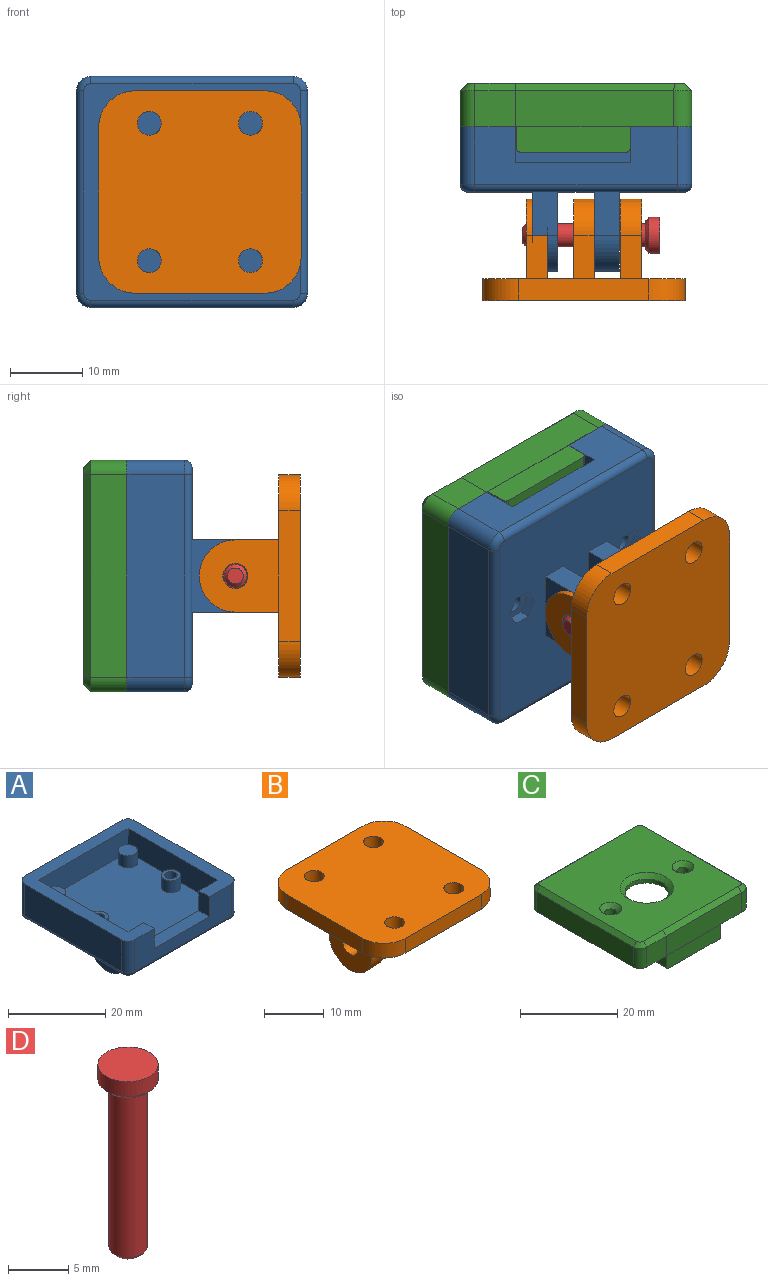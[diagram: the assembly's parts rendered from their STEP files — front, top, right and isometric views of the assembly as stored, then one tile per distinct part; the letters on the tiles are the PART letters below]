
ASSEMBLY  parts=4 mates=3
PART A: 62 faces, bbox 32.3x32.3x20 mm
  f0: plane 30x30mm, normal (0,0,-1), area 798.6mm2, adj f28,f29,f30,f31,f32,f33,f34,f35
  f1: cylinder r=1.25mm len=4.5mm, axis (0,0,-1), area 35.3mm2, adj f14,f61
  f2: cylinder r=1.25mm len=4.5mm, axis (0,0,-1), area 35.3mm2, adj f16,f54
  f3: plane 32x32mm, normal (0,0,1), area 296.6mm2, adj f4,f6,f7,f8,f9,f10,f11,f12
  f4: plane 28x8mm, normal (0,-1,0), area 144mm2, adj f3,f21,f22,f23,f26,f27,f44
  f5: plane 26x26mm, normal (0,0,1), area 625.7mm2, adj f6,f7,f8,f9,f13,f15,f17,f19
  f6: plane 26x6mm, normal (0,-1,0), area 156mm2, adj f3,f5,f7,f9
  f7: plane 26x6mm, normal (1,0,0), area 156mm2, adj f3,f5,f6,f8
  f8: plane 26x6mm, normal (0,1,0), area 76mm2, adj f3,f5,f7,f9,f21,f22,f23
  f9: plane 26x6mm, normal (-1,0,0), area 156mm2, adj f3,f5,f6,f8
  f10: plane 28x8mm, normal (1,0,0), area 224mm2, adj f3,f24,f27,f40
  f11: plane 28x8mm, normal (0,1,0), area 224mm2, adj f3,f24,f25,f43
  f12: plane 28x8mm, normal (-1,0,0), area 224mm2, adj f3,f25,f26,f47
  f13: cylinder r=2mm len=4mm, axis (0,0,-1), area 37.7mm2, adj f5,f14
  f14: plane 4x4mm, normal (0,0,1), area 7.7mm2, adj f1,f13
  f15: cylinder r=2mm len=4mm, axis (0,0,-1), area 37.7mm2, adj f5,f16
  f16: plane 4x4mm, normal (0,0,1), area 7.7mm2, adj f2,f15
  f17: cylinder r=2mm len=4mm, axis (0,0,-1), area 37.7mm2, adj f5,f18
  f18: plane 4x4mm, normal (0,0,1), area 12.6mm2, adj f17
  f19: cylinder r=2mm len=4mm, axis (0,0,-1), area 37.7mm2, adj f5,f20
  f20: plane 4x4mm, normal (0,0,1), area 12.6mm2, adj f19
  f21: plane 5x3mm, normal (1,0,0), area 15mm2, adj f3,f4,f8,f22
  f22: plane 16x3mm, normal (0,0,1), area 48mm2, adj f4,f8,f21,f23
  f23: plane 5x3mm, normal (-1,0,0), area 15mm2, adj f3,f4,f8,f22
  f24: cylinder r=2mm len=8mm, axis (0,0,-1), area 25.1mm2, adj f3,f10,f11,f41
  f25: cylinder r=2mm len=8mm, axis (0,0,1), area 25.1mm2, adj f3,f11,f12,f45
  f26: cylinder r=2mm len=8mm, axis (0,0,-1), area 25.1mm2, adj f3,f4,f12,f46
  f27: cylinder r=2mm len=8mm, axis (0,0,1), area 25.1mm2, adj f3,f4,f10,f42
  f28: plane 11x10mm, normal (1,0,0), area 89.6mm2, adj f0,f29,f31,f36,f39
  f29: plane 6x3.5mm, normal (0,1,0), area 21mm2, adj f0,f28,f30,f36
  f30: plane 11x10mm, normal (-1,0,0), area 89.6mm2, adj f0,f29,f31,f36,f39
  f31: plane 6x3.5mm, normal (0,-1,0), area 21mm2, adj f0,f28,f30,f36
  f32: plane 11x10mm, normal (1,0,0), area 89.6mm2, adj f0,f33,f35,f37,f38
  f33: plane 6x3.5mm, normal (0,1,0), area 21mm2, adj f0,f32,f34,f37
  f34: plane 11x10mm, normal (-1,0,0), area 89.6mm2, adj f0,f33,f35,f37,f38
  f35: plane 6x3.5mm, normal (0,-1,0), area 21mm2, adj f0,f32,f34,f37
  f36: cylinder r=5mm len=10mm, axis (-1,0,0), area 55mm2, adj f28,f29,f30,f31
  f37: cylinder r=5mm len=10mm, axis (-1,0,0), area 55mm2, adj f32,f33,f34,f35
  f38: cylinder r=1.75mm len=3.5mm, axis (1,0,0), area 38.5mm2, adj f32,f34
  f39: cylinder r=1.75mm len=3.5mm, axis (1,0,0), area 38.5mm2, adj f28,f30
  f40: cylinder r=1mm len=28mm, axis (0,1,0), area 44mm2, adj f0,f10,f41,f42
  f41: torus R=1mm, axis (0,0,1), area 4mm2, adj f0,f24,f40,f43
  f42: torus R=1mm, axis (0,0,1), area 4mm2, adj f0,f27,f40,f44
  f43: cylinder r=1mm len=28mm, axis (-1,0,0), area 44mm2, adj f0,f11,f41,f45
  f44: cylinder r=1mm len=28mm, axis (1,0,0), area 44mm2, adj f0,f4,f42,f46
  f45: torus R=1mm, axis (0,0,1), area 4mm2, adj f0,f25,f43,f47
  f46: torus R=1mm, axis (0,0,1), area 4mm2, adj f0,f26,f44,f47
  f47: cylinder r=1mm len=28mm, axis (0,-1,0), area 44mm2, adj f0,f12,f45,f46
  f48: plane 2.43x1.5mm, normal (0,1,0), area 3.6mm2, adj f0,f49,f53,f54
  f49: plane 2.1x1.5mm, normal (0.87,0.5,0), area 3.6mm2, adj f0,f48,f50,f54
  f50: plane 2.1x1.5mm, normal (0.87,-0.5,0), area 3.6mm2, adj f0,f49,f51,f54
  f51: plane 2.43x1.5mm, normal (0,-1,0), area 3.6mm2, adj f0,f50,f52,f54
  f52: plane 2.1x1.5mm, normal (-0.87,-0.5,0), area 3.6mm2, adj f0,f51,f53,f54
  f53: plane 2.1x1.5mm, normal (-0.87,0.5,0), area 3.6mm2, adj f0,f48,f52,f54
  f54: plane 4.85x4.2mm, normal (0,0,-1), area 10.4mm2, adj f2,f48,f49,f50,f51,f52,f53
  f55: plane 2.43x1.5mm, normal (0,1,0), area 3.6mm2, adj f0,f56,f60,f61
  f56: plane 2.1x1.5mm, normal (0.87,0.5,0), area 3.6mm2, adj f0,f55,f57,f61
  f57: plane 2.1x1.5mm, normal (0.87,-0.5,0), area 3.6mm2, adj f0,f56,f58,f61
  f58: plane 2.43x1.5mm, normal (0,-1,0), area 3.6mm2, adj f0,f57,f59,f61
  f59: plane 2.1x1.5mm, normal (-0.87,-0.5,0), area 3.6mm2, adj f0,f58,f60,f61
  f60: plane 2.1x1.5mm, normal (-0.87,0.5,0), area 3.6mm2, adj f0,f55,f59,f61
  f61: plane 4.85x4.2mm, normal (0,0,-1), area 10.4mm2, adj f1,f55,f56,f57,f58,f59,f60
PART B: 32 faces, bbox 28x28x14 mm
  f0: plane 18x3mm, normal (0,-1,0), area 54mm2, adj f4,f5,f28,f31
  f1: plane 18x3mm, normal (1,0,0), area 54mm2, adj f4,f5,f28,f29
  f2: plane 18x3mm, normal (0,1,0), area 54mm2, adj f4,f5,f29,f30
  f3: plane 18x3mm, normal (-1,0,0), area 54mm2, adj f4,f5,f30,f31
  f4: plane 28x28mm, normal (0,0,-1), area 640.3mm2, adj f0,f1,f2,f3,f6,f7,f8,f9
  f5: plane 28x28mm, normal (0,0,1), area 728.3mm2, adj f0,f1,f2,f3,f24,f25,f26,f27
  f6: plane 6x2.8mm, normal (0,-1,0), area 16.8mm2, adj f4,f7,f9,f19
  f7: plane 11x10mm, normal (-1,0,0), area 89.6mm2, adj f4,f6,f8,f19,f23
  f8: plane 6x2.8mm, normal (0,1,0), area 16.8mm2, adj f4,f7,f9,f19
  f9: plane 11x10mm, normal (1,0,0), area 89.6mm2, adj f4,f6,f8,f19,f23
  f10: plane 11x10mm, normal (1,0,0), area 89.6mm2, adj f4,f11,f13,f20,f22
  f11: plane 6x3mm, normal (0,-1,0), area 18mm2, adj f4,f10,f12,f20
  f12: plane 11x10mm, normal (-1,0,0), area 89.6mm2, adj f4,f11,f13,f20,f22
  f13: plane 6x3mm, normal (0,1,0), area 18mm2, adj f4,f10,f12,f20
  f14: plane 6x3mm, normal (0,-1,0), area 18mm2, adj f4,f15,f17,f18
  f15: plane 11x10mm, normal (-1,0,0), area 89.6mm2, adj f4,f14,f16,f18,f21
  f16: plane 6x3mm, normal (0,1,0), area 18mm2, adj f4,f15,f17,f18
  f17: plane 11x10mm, normal (1,0,0), area 89.6mm2, adj f4,f14,f16,f18,f21
  f18: cylinder r=5mm len=10mm, axis (1,0,0), area 47.1mm2, adj f14,f15,f16,f17
  f19: cylinder r=5mm len=10mm, axis (1,0,0), area 44mm2, adj f6,f7,f8,f9
  f20: cylinder r=5mm len=10mm, axis (-1,0,0), area 47.1mm2, adj f10,f11,f12,f13
  f21: cylinder r=1.75mm len=3.5mm, axis (1,0,0), area 33mm2, adj f15,f17
  f22: cylinder r=1.75mm len=3.5mm, axis (1,0,0), area 33mm2, adj f10,f12
  f23: cylinder r=1.75mm len=3.5mm, axis (1,0,0), area 30.8mm2, adj f7,f9
  f24: cylinder r=1.65mm len=3.3mm, axis (0,0,-1), area 31.1mm2, adj f4,f5
  f25: cylinder r=1.65mm len=3.3mm, axis (0,0,-1), area 31.1mm2, adj f4,f5
  f26: cylinder r=1.65mm len=3.3mm, axis (0,0,-1), area 31.1mm2, adj f4,f5
  f27: cylinder r=1.65mm len=3.3mm, axis (0,0,-1), area 31.1mm2, adj f4,f5
  f28: cylinder r=5mm len=5mm, axis (0,0,-1), area 23.6mm2, adj f0,f1,f4,f5
  f29: cylinder r=5mm len=5mm, axis (0,0,1), area 23.6mm2, adj f1,f2,f4,f5
  f30: cylinder r=5mm len=5mm, axis (0,0,-1), area 23.6mm2, adj f2,f3,f4,f5
  f31: cylinder r=5mm len=5mm, axis (0,0,1), area 23.6mm2, adj f0,f3,f4,f5
PART C: 48 faces, bbox 32x32x9.5 mm
  f0: cylinder r=4.5mm len=9mm, axis (0,0,1), area 28.3mm2, adj f28,f40
  f1: plane 26x26mm, normal (0,0,-1), area 398.8mm2, adj f3,f4,f5,f14,f17,f20,f23,f25
  f2: plane 30x30mm, normal (0,0,1), area 771.6mm2, adj f29,f30,f31,f32,f33,f34,f35,f36
  f3: plane 26x3mm, normal (0,-1,0), area 78mm2, adj f1,f4,f5,f16
  f4: plane 26x3mm, normal (1,0,0), area 78mm2, adj f1,f3,f14,f16
  f5: plane 26x3mm, normal (-1,0,0), area 78mm2, adj f1,f3,f14,f16
  f6: plane 28x5mm, normal (1,0,0), area 140mm2, adj f7,f15,f16,f35
  f7: cylinder r=2mm len=5mm, axis (0,0,1), area 15.7mm2, adj f6,f8,f16,f33
  f8: plane 28x5mm, normal (0,1,0), area 140mm2, adj f7,f9,f16,f31
  f9: cylinder r=2mm len=5mm, axis (0,0,1), area 15.7mm2, adj f8,f10,f16,f32
  f10: plane 28x5mm, normal (-1,0,0), area 140mm2, adj f9,f11,f16,f34
  f11: cylinder r=2mm len=5mm, axis (0,0,1), area 15.7mm2, adj f10,f12,f16,f36
  f12: plane 5.6x5mm, normal (0,-1,0), area 28mm2, adj f11,f13,f16,f38
  f13: plane 21.92x5mm, normal (0,-1,0), area 109.6mm2, adj f12,f15,f16,f39,f41
  f14: plane 26x6.5mm, normal (0,1,0), area 132.8mm2, adj f1,f4,f5,f16,f43,f44,f45,f46
  f15: cylinder r=2mm len=5mm, axis (0,0,1), area 18.2mm2, adj f6,f13,f16,f37
  f16: plane 32x32mm, normal (0,0,-1), area 297.1mm2, adj f3,f4,f5,f6,f7,f8,f9,f10
  f17: cylinder r=2mm len=5mm, axis (0,0,1), area 62.8mm2, adj f1,f19
  f18: cylinder r=1.25mm len=7mm, axis (0,0,1), area 55mm2, adj f19,f30
  f19: plane 4x4mm, normal (0,0,-1), area 7.7mm2, adj f17,f18
  f20: cylinder r=2mm len=5mm, axis (0,0,1), area 62.8mm2, adj f1,f22
  f21: cylinder r=1.25mm len=7mm, axis (0,0,1), area 55mm2, adj f22,f29
  f22: plane 4x4mm, normal (0,0,-1), area 7.7mm2, adj f20,f21
  f23: cylinder r=2mm len=5mm, axis (0,0,1), area 62.8mm2, adj f1,f24
  f24: plane 4x4mm, normal (0,0,-1), area 12.6mm2, adj f23
  f25: cylinder r=2mm len=5mm, axis (0,0,1), area 62.8mm2, adj f1,f26
  f26: plane 4x4mm, normal (0,0,-1), area 12.6mm2, adj f25
  f27: cylinder r=8.5mm len=17mm, axis (0,0,-1), area 53.4mm2, adj f1,f28
  f28: plane 17x17mm, normal (0,0,-1), area 163.4mm2, adj f0,f27
  f29: cone r=1.25mm half-angle=45deg, axis (0,0,1), area 15.6mm2, adj f2,f21
  f30: cone r=1.25mm half-angle=45deg, axis (0,0,1), area 15.6mm2, adj f2,f18
  f31: plane 28x1mm, normal (0,0.71,0.71), area 39.6mm2, adj f2,f8,f32,f33
  f32: cone r=1mm half-angle=45deg, axis (0,0,-1), area 3.3mm2, adj f2,f9,f31,f34
  f33: cone r=1mm half-angle=45deg, axis (0,0,-1), area 3.3mm2, adj f2,f7,f31,f35
  f34: plane 28x1mm, normal (-0.71,0,0.71), area 39.6mm2, adj f2,f10,f32,f36
  f35: plane 28x1mm, normal (0.71,0,0.71), area 39.6mm2, adj f2,f6,f33,f37
  f36: cone r=1mm half-angle=45deg, axis (0,0,-1), area 3.3mm2, adj f2,f11,f34,f38
  f37: cone r=1mm half-angle=45deg, axis (0,0,-1), area 3.9mm2, adj f2,f15,f35,f39
  f38: plane 5.6x1mm, normal (0,-0.71,0.71), area 7.9mm2, adj f2,f12,f36,f39
  f39: plane 22.1x1.1mm, normal (0,-0.71,0.71), area 31.1mm2, adj f2,f13,f37,f38
  f40: cone r=4.5mm half-angle=45deg, axis (0,0,1), area 44.4mm2, adj f0,f2
  f41: plane 15.7x0.04mm, normal (0,0,1), area 0.3mm2, adj f13,f42,f44
  f42: plane 15.7x3.5mm, normal (0,-1,0), area 54.8mm2, adj f41,f43,f44,f45,f46,f47
  f43: plane 3x3mm, normal (-1,0,0), area 9mm2, adj f14,f16,f42,f47
  f44: plane 3x3mm, normal (1,0,0), area 9mm2, adj f14,f16,f41,f42,f46
  f45: plane 14.7x3mm, normal (0,0,-1), area 44.1mm2, adj f14,f42,f46,f47
  f46: cylinder r=0.5mm len=3mm, axis (0,1,0), area 2.4mm2, adj f14,f42,f44,f45
  f47: cylinder r=0.5mm len=3mm, axis (0,-1,0), area 2.4mm2, adj f14,f42,f43,f45
PART D: 7 faces, bbox 5x5x19 mm
  f0: cylinder r=2.5mm len=5mm, axis (0,0,1), area 23.6mm2, adj f2,f3
  f1: plane 4x4mm, normal (0,0,-1), area 4.5mm2, adj f3,f4
  f2: plane 5x5mm, normal (0,0,1), area 19.6mm2, adj f0
  f3: cone r=2.5mm half-angle=45deg, axis (0,0,1), area 10mm2, adj f0,f1
  f4: cylinder r=1.6mm len=16.5mm, axis (0,0,1), area 165.9mm2, adj f1,f6
  f5: plane 2.2x2.2mm, normal (0,0,-1), area 3.8mm2, adj f6
  f6: cone r=1.1mm half-angle=45deg, axis (0,0,1), area 6mm2, adj f4,f5
PLACE A rot(axis=(-1,0,0),90deg) t=(-15,0,2)mm
PLACE B rot(axis=(1,0,0),90deg) t=(43.27,-15,-12)mm
PLACE C rot(axis=(-1,0,0),90deg) t=(-15,-19,2)mm
PLACE D rot(axis=(0,1,0),90deg) t=(-3.4,14.72,-55.53)mm
MATE fastened C.f16 <-> A.f3  axis (0,1,0) through (-1,9,-14)mm
MATE fastened B.f18 <-> A.f38  axis (1,0,0) through (-12.5,-6,2)mm
MATE pin_slot D.f0 <-> B.f18  axis (-1,0,0) through (-21.9,-6,2)mm
